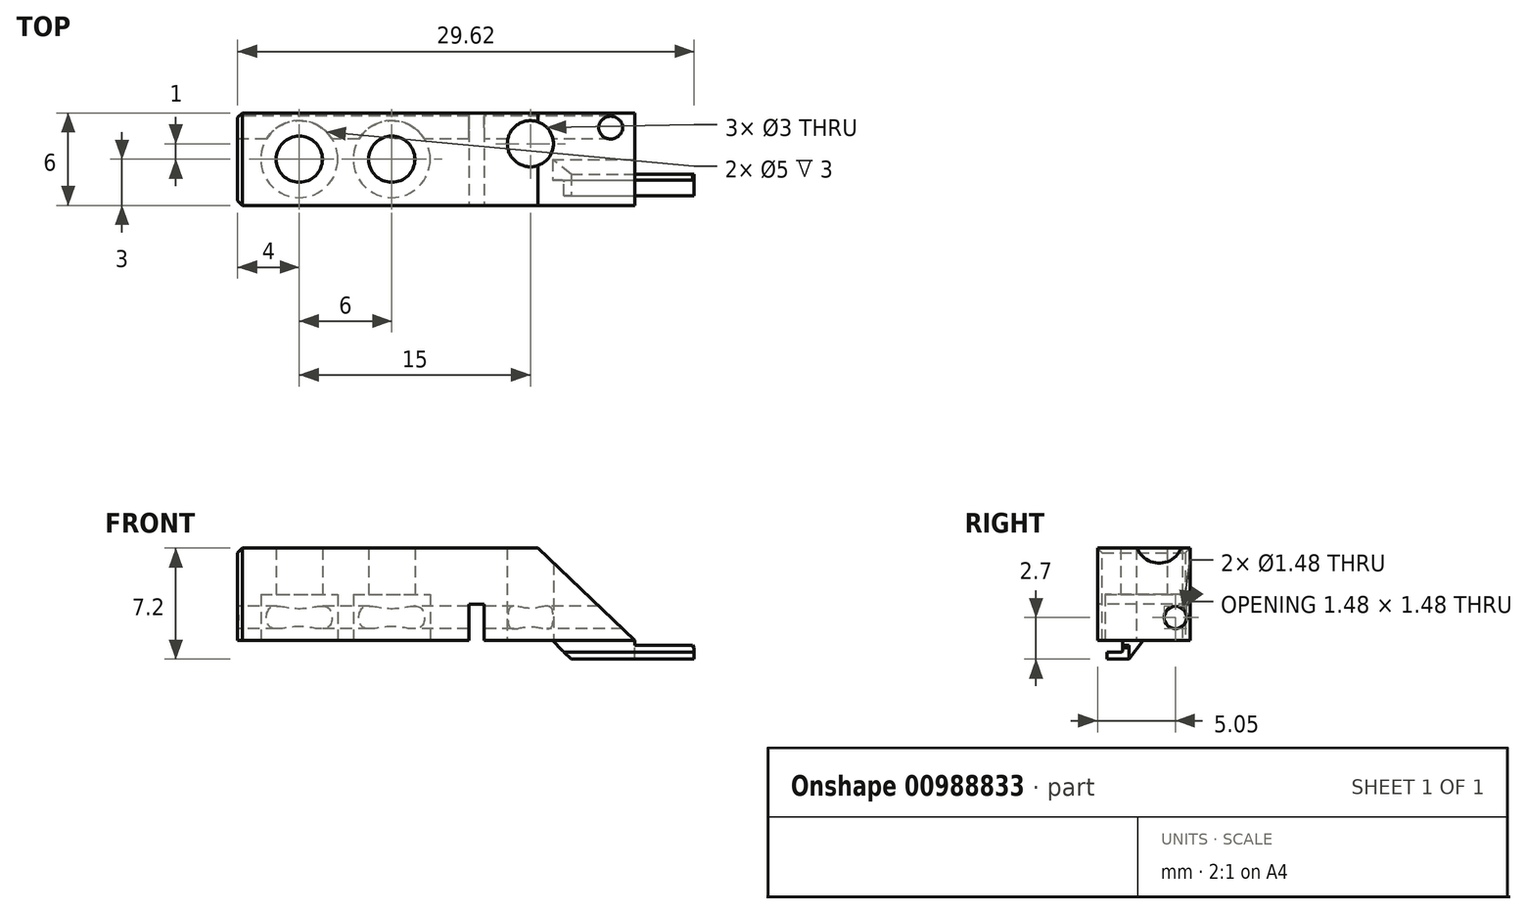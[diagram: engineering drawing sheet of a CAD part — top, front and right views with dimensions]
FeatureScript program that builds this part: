
annotation { "Feature Type Name" : "Feature", "Feature Type Description" : "" }
export const myFeature = defineFeature(function(context is Context, id is Id, definition is map)
    precondition{}
    {
        {
            var Q0;
            Q0=qCreatedBy(makeId("Front.planeOp"),FACE);
            var sketch = newSketch(context, id + "F0", { "sketchPlane" : qUnion([Q0])});
            skLineSegment(sketch, "E0.bottom", {"start": v(14.8, -3.6) * mm, "end": v(-14.8, -3.6) * mm});
            skLineSegment(sketch, "E0.top", {"start": v(14.8, 3.6) * mm, "end": v(-14.8, 3.6) * mm});
            skLineSegment(sketch, "E0.left", {"start": v(14.8, -3.6) * mm, "end": v(14.8, 3.6) * mm});
            skLineSegment(sketch, "E0.right", {"start": v(-14.8, -3.6) * mm, "end": v(-14.8, 3.6) * mm});
            skPoint(sketch, "E0.middle", {"position": v(0, 0) * mm});
            skSolve(sketch);
        }
        {
            var Q0;
            Q0 = qSketchRegion(id + "F0", true);
            extrude(context, id + "F1", {"entities" : qUnion([Q0]), "oppositeDirection" : true, "depth" : 6 * mm, "offsetDistance" : 25 * mm});
        }
        {
            var Q0;
            Q0=makeQuery(id+"F1.opExtrude","CAP_FACE",FACE,{"disambiguationData":[OSD([sQuery(id+"F0.wireOp",EDGE,"E0.bottom"),sQuery(id+"F0.wireOp",EDGE,"E0.top"),sQuery(id+"F0.wireOp",EDGE,"E0.left"),sQuery(id+"F0.wireOp",EDGE,"E0.right")])],"isStart":true});
            var sketch = newSketch(context, id + "F2", { "sketchPlane" : qUnion([Q0])});
            skLineSegment(sketch, "E1", {"start": v(14.8, -3.6) * mm, "end": v(14.8, -2.4) * mm});
            skLineSegment(sketch, "E2", {"start": v(14.8, -2.4) * mm, "end": v(10.97, -2.4) * mm});
            skLineSegment(sketch, "E3", {"start": v(14.8, 3.6) * mm, "end": v(4.67, 3.6) * mm});
            skLineSegment(sketch, "E4", {"start": v(4.67, 3.6) * mm, "end": v(10.97, -2.4) * mm});
            skLineSegment(sketch, "E5", {"start": v(14.8, -2.4) * mm, "end": v(14.8, 3.6) * mm});
            skSolve(sketch);
        }
        {
            var Q0;
            Q0 = qSketchRegion(id + "F2", true);
            extrude(context, id + "F3", {"entities" : qUnion([Q0]), "operationType" : NewBodyOperationType.REMOVE, "endBound" : BoundingType.UP_TO_NEXT, "oppositeDirection" : true, "depth" : 25 * mm, "offsetDistance" : 25 * mm});
        }
        {
            var Q0;
            Q0=makeQuery(id+"F1.opExtrude","CAP_FACE",FACE,{"disambiguationData":[OSD([sQuery(id+"F0.wireOp",EDGE,"E0.bottom"),sQuery(id+"F0.wireOp",EDGE,"E0.top"),sQuery(id+"F0.wireOp",EDGE,"E0.left"),sQuery(id+"F0.wireOp",EDGE,"E0.right")])],"isStart":true});
            var sketch = newSketch(context, id + "F4", { "sketchPlane" : qUnion([Q0])});
            skLineSegment(sketch, "E6", {"start": v(5.62, -2.4) * mm, "end": v(6.82, -3.6) * mm});
            skLineSegment(sketch, "E7", {"start": v(5.62, -2.4) * mm, "end": v(-14.8, -2.4) * mm});
            skLineSegment(sketch, "E8", {"start": v(-14.8, -2.4) * mm, "end": v(-14.8, -3.6) * mm});
            skLineSegment(sketch, "E9", {"start": v(-14.8, -3.6) * mm, "end": v(6.82, -3.6) * mm});
            skSolve(sketch);
        }
        {
            var Q0;
            Q0 = qSketchRegion(id + "F4", true);
            extrude(context, id + "F5", {"entities" : qUnion([Q0]), "operationType" : NewBodyOperationType.REMOVE, "endBound" : BoundingType.UP_TO_NEXT, "oppositeDirection" : true, "depth" : 25 * mm, "offsetDistance" : 25 * mm});
        }
        {
            var Q0;
            Q0=makeQuery(id+"F5.boolean.opBoolean","COPY",FACE,{"derivedFrom":makeQuery(id+"F5.opExtrude","SWEPT_FACE",FACE,{"disambiguationData":[OSD([sQuery(id+"F4.wireOp",EDGE,"E7")])]})});
            var sketch = newSketch(context, id + "F6", { "sketchPlane" : qUnion([Q0])});
            skLineSegment(sketch, "E10", {"start": v(-14.8, -6) * mm, "end": v(0.19, -6) * mm});
            skLineSegment(sketch, "E11.bottom", {"start": v(0.19, -6) * mm, "end": v(1.19, -6) * mm});
            skLineSegment(sketch, "E11.top", {"start": v(0.19, 0) * mm, "end": v(1.19, 0) * mm});
            skLineSegment(sketch, "E11.left", {"start": v(0.19, -6) * mm, "end": v(0.19, 0) * mm});
            skLineSegment(sketch, "E11.right", {"start": v(1.19, -6) * mm, "end": v(1.19, 0) * mm});
            skSolve(sketch);
        }
        {
            var Q0;
            Q0 = qSketchRegion(id + "F6", true);
            extrude(context, id + "F7", {"entities" : qUnion([Q0]), "operationType" : NewBodyOperationType.REMOVE, "oppositeDirection" : true, "depth" : (6 - 3.65) * mm, "offsetDistance" : 25 * mm});
        }
        {
            var Q0;
            Q0=makeQuery(id+"F1.opExtrude","SWEPT_FACE",FACE,{"disambiguationData":[OSD([sQuery(id+"F0.wireOp",EDGE,"E0.left")])]});
            var sketch = newSketch(context, id + "F8", { "sketchPlane" : qUnion([Q0])});
            skLineSegment(sketch, "E12.bottom", {"start": v(6, -3.6) * mm, "end": v(2.98, -3.6) * mm});
            skLineSegment(sketch, "E12.top", {"start": v(6, -2.4) * mm, "end": v(2.98, -2.4) * mm});
            skLineSegment(sketch, "E12.left", {"start": v(6, -3.6) * mm, "end": v(6, -2.4) * mm});
            skLineSegment(sketch, "E12.right", {"start": v(2.98, -3.6) * mm, "end": v(2.98, -2.4) * mm});
            skSolve(sketch);
        }
        {
            var Q0;
            Q0 = qSketchRegion(id + "F8", true);
            extrude(context, id + "F9", {"entities" : qUnion([Q0]), "operationType" : NewBodyOperationType.REMOVE, "endBound" : BoundingType.UP_TO_NEXT, "oppositeDirection" : true, "depth" : 25 * mm, "offsetDistance" : 25 * mm});
        }
        {
            var Q0;
            Q0=makeQuery(id+"F1.opExtrude","SWEPT_FACE",FACE,{"disambiguationData":[OSD([sQuery(id+"F0.wireOp",EDGE,"E0.left")])]});
            var sketch = newSketch(context, id + "F10", { "sketchPlane" : qUnion([Q0])});
            skLineSegment(sketch, "E13", {"start": v(2.98, -3.6) * mm, "end": v(2.03, -3.6) * mm});
            skLineSegment(sketch, "E14", {"start": v(2.03, -3.6) * mm, "end": v(2.98, -2.4) * mm});
            skLineSegment(sketch, "E15", {"start": v(2.98, -2.4) * mm, "end": v(2.98, -3.6) * mm});
            skSolve(sketch);
        }
        {
            var Q0;
            Q0 = qSketchRegion(id + "F10", true);
            extrude(context, id + "F11", {"entities" : qUnion([Q0]), "operationType" : NewBodyOperationType.REMOVE, "endBound" : BoundingType.UP_TO_NEXT, "oppositeDirection" : true, "depth" : 25 * mm, "offsetDistance" : 25 * mm});
        }
        {
            var Q0;
            Q0=makeQuery(id+"F1.opExtrude","SWEPT_FACE",FACE,{"disambiguationData":[OSD([sQuery(id+"F0.wireOp",EDGE,"E0.left")])]});
            var sketch = newSketch(context, id + "F12", { "sketchPlane" : qUnion([Q0])});
            skLineSegment(sketch, "E16", {"start": v(2.03, -3.6) * mm, "end": v(0.63, -3.6) * mm});
            skLineSegment(sketch, "E17", {"start": v(0.63, -3.6) * mm, "end": v(0.63, -3.15) * mm});
            skLineSegment(sketch, "E18", {"start": v(0.63, -3.15) * mm, "end": v(1.63, -3.15) * mm});
            skLineSegment(sketch, "E19.bottom", {"start": v(1.63, -3.15) * mm, "end": v(0, -3.15) * mm});
            skLineSegment(sketch, "E19.top", {"start": v(1.63, -2.4) * mm, "end": v(0, -2.4) * mm});
            skLineSegment(sketch, "E19.left", {"start": v(1.63, -3.15) * mm, "end": v(1.63, -2.4) * mm});
            skLineSegment(sketch, "E19.right", {"start": v(0, -3.15) * mm, "end": v(0, -2.4) * mm});
            skLineSegment(sketch, "E20.bottom", {"start": v(0, -3.6) * mm, "end": v(0.63, -3.6) * mm});
            skLineSegment(sketch, "E20.top", {"start": v(0, -3.15) * mm, "end": v(0.63, -3.15) * mm});
            skLineSegment(sketch, "E20.left", {"start": v(0, -3.6) * mm, "end": v(0, -3.15) * mm});
            skSolve(sketch);
        }
        {
            var Q0;
            Q0 = qSketchRegion(id + "F12", true);
            extrude(context, id + "F13", {"entities" : qUnion([Q0]), "operationType" : NewBodyOperationType.REMOVE, "endBound" : BoundingType.UP_TO_NEXT, "oppositeDirection" : true, "depth" : 25 * mm, "offsetDistance" : 25 * mm});
        }
        {
            var Q0;
            Q0=makeQuery(id+"F13.boolean.opBoolean","COPY",EDGE,{"derivedFrom":makeQuery(id+"F13.opExtrude","SWEPT_EDGE",EDGE,{"disambiguationData":[OSD([sQuery(id+"F12.wireOp",EDGE,"E19.bottom"),sQuery(id+"F12.wireOp",EDGE,"E19.left")])]})});
            fillet(context, id + "F14", {"entities" : qUnion([Q0]), "radius" : .1 * mm, "tangentPropagation" : true, "allowEdgeOverflow" : false});
        }
        {
            var Q0;
            Q0=makeQuery(id+"F1.opExtrude","SWEPT_FACE",FACE,{"disambiguationData":[OSD([sQuery(id+"F0.wireOp",EDGE,"E0.left")])]});
            var sketch = newSketch(context, id + "F15", { "sketchPlane" : qUnion([Q0])});
            skLineSegment(sketch, "E21", {"start": v(2.03, -3.6) * mm, "end": v(2.03, -2.7) * mm});
            skLineSegment(sketch, "E22", {"start": v(2.03, -2.7) * mm, "end": v(1.63, -2.7) * mm});
            skPoint(sketch, "E22.endSnap0", {"position": v(1.63, -2.73) * mm});
            skLineSegment(sketch, "E23", {"start": v(1.63, -2.7) * mm, "end": v(1.63, -2.4) * mm});
            skLineSegment(sketch, "E24", {"start": v(1.63, -2.4) * mm, "end": v(2.98, -2.4) * mm});
            skLineSegment(sketch, "E25", {"start": v(2.98, -2.4) * mm, "end": v(2.03, -3.6) * mm});
            skSolve(sketch);
        }
        {
            var Q0;
            Q0 = qSketchRegion(id + "F15", true);
            extrude(context, id + "F16", {"entities" : qUnion([Q0]), "operationType" : NewBodyOperationType.REMOVE, "oppositeDirection" : true, "depth" : 3.84 * mm, "offsetDistance" : 25 * mm});
        }
        {
            var Q0;
            Q0=makeQuery(id+"F13.boolean.opBoolean","COPY",FACE,{"derivedFrom":makeQuery(id+"F13.opExtrude","SWEPT_FACE",FACE,{"disambiguationData":[OSD([sQuery(id+"F12.wireOp",EDGE,"E19.left")])]})});
            var sketch = newSketch(context, id + "F17", { "sketchPlane" : qUnion([Q0])});
            skLineSegment(sketch, "E26", {"start": v(14.8, -2.7) * mm, "end": v(14.71, -2.7) * mm});
            skLineSegment(sketch, "E27", {"start": v(14.71, -2.7) * mm, "end": v(14.87, -2.98) * mm});
            skLineSegment(sketch, "E28", {"start": v(14.8, -2.7) * mm, "end": v(14.8, -2.87) * mm});
            skSolve(sketch);
        }
        {
            var Q0;
            Q0 = qSketchRegion(id + "F17", true);
            extrude(context, id + "F18", {"entities" : qUnion([Q0]), "operationType" : NewBodyOperationType.REMOVE, "endBound" : BoundingType.UP_TO_NEXT, "oppositeDirection" : true, "depth" : 25 * mm, "offsetDistance" : 25 * mm});
        }
        {
            var Q0;
            {var subQ0=sQuery(id+"F0.wireOp",EDGE,"E0.right");Q0=makeQuery(id+"F7.boolean.opBoolean","SPLIT",FACE,{"disambiguationData":[TD([makeQuery(id+"F1.opExtrude","SWEPT_FACE",FACE,{"disambiguationData":[OSD([subQ0])]})])],"derivedFrom":makeQuery(id+"F5.boolean.opBoolean","COPY",FACE,{"derivedFrom":makeQuery(id+"F5.opExtrude","SWEPT_FACE",FACE,{"disambiguationData":[OSD([sQuery(id+"F4.wireOp",EDGE,"E7")])]})})});}
            var sketch = newSketch(context, id + "F19", { "sketchPlane" : qUnion([Q0])});
            skLineSegment(sketch, "E29", {"start": v(-14.8, -6) * mm, "end": v(-10.8, -6) * mm});
            skLineSegment(sketch, "E30", {"start": v(-10.8, -6) * mm, "end": v(-4.8, -6) * mm});
            skLineSegment(sketch, "E31", {"start": v(-4.8, -6) * mm, "end": v(-4.8, -3) * mm});
            skLineSegment(sketch, "E32", {"start": v(-10.8, -6) * mm, "end": v(-10.8, -3) * mm});
            skCircle(sketch, "E33", {"center": v(-10.8, -3) * mm, "radius": 1.5 * mm});
            skCircle(sketch, "E34", {"center": v(-4.8, -3) * mm, "radius": 1.5 * mm});
            skSolve(sketch);
        }
        {
            var Q0;
            Q0 = qSketchRegion(id + "F19", true);
            extrude(context, id + "F20", {"entities" : qUnion([Q0]), "operationType" : NewBodyOperationType.REMOVE, "endBound" : BoundingType.UP_TO_NEXT, "oppositeDirection" : true, "depth" : 25 * mm, "offsetDistance" : 25 * mm});
        }
        {
            var Q0;
            {var subQ0=sQuery(id+"F0.wireOp",EDGE,"E0.right");Q0=makeQuery(id+"F7.boolean.opBoolean","SPLIT",FACE,{"disambiguationData":[TD([makeQuery(id+"F1.opExtrude","SWEPT_FACE",FACE,{"disambiguationData":[OSD([subQ0])]})])],"derivedFrom":makeQuery(id+"F5.boolean.opBoolean","COPY",FACE,{"derivedFrom":makeQuery(id+"F5.opExtrude","SWEPT_FACE",FACE,{"disambiguationData":[OSD([sQuery(id+"F4.wireOp",EDGE,"E7")])]})})});}
            var sketch = newSketch(context, id + "F21", { "sketchPlane" : qUnion([Q0])});
            skCircle(sketch, "E35", {"center": v(-10.8, -3) * mm, "radius": 2.5 * mm});
            skCircle(sketch, "E36", {"center": v(-4.8, -3) * mm, "radius": 2.5 * mm});
            skSolve(sketch);
        }
        {
            var Q0;
            Q0 = qSketchRegion(id + "F21", true);
            extrude(context, id + "F22", {"entities" : qUnion([Q0]), "operationType" : NewBodyOperationType.REMOVE, "oppositeDirection" : true, "depth" : 3 * mm, "offsetDistance" : 25 * mm});
        }
        {
            var Q0;
            Q0=makeQuery(id+"F1.opExtrude","SWEPT_FACE",FACE,{"disambiguationData":[OSD([sQuery(id+"F0.wireOp",EDGE,"E0.right")])]});
            var sketch = newSketch(context, id + "F23", { "sketchPlane" : qUnion([Q0])});
            skLineSegment(sketch, "E37", {"start": v(-6, 3.6) * mm, "end": v(-6, -0.9) * mm});
            skLineSegment(sketch, "E38", {"start": v(-6, -0.9) * mm, "end": v(-5.05, -0.9) * mm});
            skCircle(sketch, "E39", {"center": v(-5.05, -0.9) * mm, "radius": 0.74 * mm});
            skSolve(sketch);
        }
        {
            var Q0;
            Q0 = qSketchRegion(id + "F23", true);
            extrude(context, id + "F24", {"entities" : qUnion([Q0]), "operationType" : NewBodyOperationType.REMOVE, "endBound" : BoundingType.THROUGH_ALL, "oppositeDirection" : true, "depth" : 25 * mm, "offsetDistance" : 25 * mm});
        }
        {
            var Q0;
            Q0=makeQuery(id+"F1.opExtrude","CAP_EDGE",EDGE,{"disambiguationData":[OSD([sQuery(id+"F0.wireOp",EDGE,"E0.right")])],"isStart":true});
            var Q1;
            Q1=makeQuery(id+"F1.opExtrude","CAP_EDGE",EDGE,{"disambiguationData":[OSD([sQuery(id+"F0.wireOp",EDGE,"E0.right")])],"isStart":false});
            var Q2;
            Q2=makeQuery(id+"F1.opExtrude","SWEPT_EDGE",EDGE,{"disambiguationData":[OSD([sQuery(id+"F0.wireOp",EDGE,"E0.top"),sQuery(id+"F0.wireOp",EDGE,"E0.right")])]});
            var Q3;
            Q3=makeQuery(id+"F5.boolean.opBoolean","COPY",EDGE,{"derivedFrom":makeQuery(id+"F5.opExtrude","SWEPT_EDGE",EDGE,{"disambiguationData":[OSD([sQuery(id+"F0.wireOp",EDGE,"E0.right"),sQuery(id+"F4.wireOp",EDGE,"E7"),sQuery(id+"F4.wireOp",EDGE,"E8")])]})});
            chamfer(context, id + "F25", {"entities" : qUnion([Q0, Q1, Q2, Q3]), "width" : 0.3 * mm, "tangentPropagation" : true});
        }
        {
            var Q0;
            Q0=makeQuery(id+"F13.boolean.opBoolean","MERGE",FACE,{"derivedFrom":[makeQuery(id+"F9.boolean.opBoolean","MERGE",FACE,{"derivedFrom":[makeQuery(id+"F7.boolean.opBoolean","SPLIT",FACE,{"disambiguationData":[TD([makeQuery(id+"F5.boolean.opBoolean","COPY",FACE,{"derivedFrom":makeQuery(id+"F5.opExtrude","SWEPT_FACE",FACE,{"disambiguationData":[OSD([sQuery(id+"F4.wireOp",EDGE,"E6")])]})})])],"derivedFrom":makeQuery(id+"F5.boolean.opBoolean","COPY",FACE,{"derivedFrom":makeQuery(id+"F5.opExtrude","SWEPT_FACE",FACE,{"disambiguationData":[OSD([sQuery(id+"F4.wireOp",EDGE,"E7")])]})})})],"fromTools":[makeQuery(id+"F9.opExtrude","SWEPT_FACE",FACE,{"disambiguationData":[OSD([sQuery(id+"F8.wireOp",EDGE,"E12.top")])]})]})],"fromTools":[makeQuery(id+"F13.opExtrude","SWEPT_FACE",FACE,{"disambiguationData":[OSD([sQuery(id+"F12.wireOp",EDGE,"E19.top")])]})]});
            var sketch = newSketch(context, id + "F26", { "sketchPlane" : qUnion([Q0])});
            skLineSegment(sketch, "E40", {"start": v(1.19, -6) * mm, "end": v(4.19, -6) * mm});
            skLineSegment(sketch, "E41", {"start": v(4.19, -6) * mm, "end": v(4.19, -4) * mm});
            skCircle(sketch, "E42", {"center": v(4.19, -4) * mm, "radius": 1.5 * mm});
            skSolve(sketch);
        }
        {
            var Q0;
            Q0 = qSketchRegion(id + "F26", true);
            extrude(context, id + "F27", {"entities" : qUnion([Q0]), "operationType" : NewBodyOperationType.REMOVE, "endBound" : BoundingType.UP_TO_NEXT, "oppositeDirection" : true, "depth" : 25 * mm, "offsetDistance" : 25 * mm});
        }
    });
